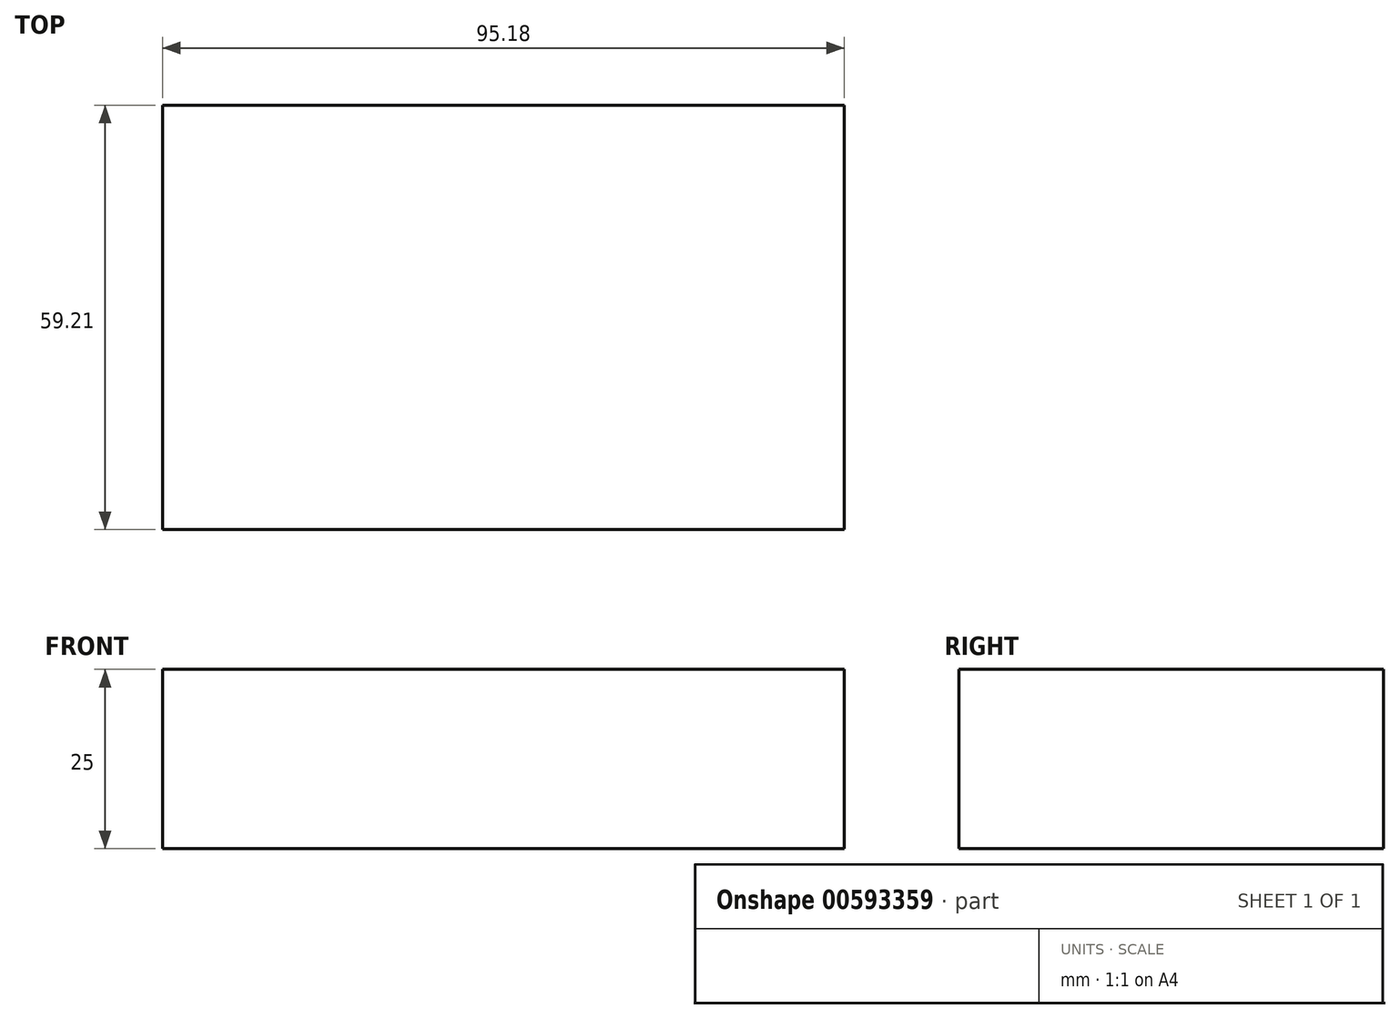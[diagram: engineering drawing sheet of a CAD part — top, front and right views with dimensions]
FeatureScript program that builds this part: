
annotation { "Feature Type Name" : "Feature", "Feature Type Description" : "" }
export const myFeature = defineFeature(function(context is Context, id is Id, definition is map)
    precondition{}
    {
        {
            var Q0;
            Q0=qCreatedBy(makeId("Top.planeOp"),FACE);
            var sketch = newSketch(context, id + "F0", { "sketchPlane" : qUnion([Q0])});
            skLineSegment(sketch, "E0.bottom", {"start": v(-38.1, 29.04) * mm, "end": v(57.08, 29.04) * mm});
            skLineSegment(sketch, "E0.top", {"start": v(-38.1, -30.17) * mm, "end": v(57.08, -30.17) * mm});
            skLineSegment(sketch, "E0.left", {"start": v(-38.1, 29.04) * mm, "end": v(-38.1, -30.17) * mm});
            skLineSegment(sketch, "E0.right", {"start": v(57.08, 29.04) * mm, "end": v(57.08, -30.17) * mm});
            skSolve(sketch);
        }
        {
            var Q0;
            Q0 = qSketchRegion(id + "F0", true);
            extrude(context, id + "F1", {"entities" : qUnion([Q0]), "endBound" : BoundingType.SYMMETRIC, "depth" : 25 * mm, "offsetDistance" : 25 * mm});
        }
    });
